# Revit family: Specialty-Equipment_TheSplashLab_Bath-Grab-Bars_GR-45-36
name_source: partatom
category: Specialty Equipment
revit_build: Autodesk Revit 2016 (Build: 20160314_0715(x64)
units: mm (PartAtom-declared; Revit-internal decimal feet)

## family parameters
Cut with Voids When Loaded = No
Host = Face
OmniClass Number = 23.40.20.21.47
OmniClass Title = Bath Grab Bars
Part Type = Normal
Room Calculation Point = No
Round Connector Dimension = Use Diameter
Shared = No

## types (5) — shared parameters
Assembly Code = E1090
AssetType = Fixed
BIMObjectName = Specialty-Equipment_TheSplashLab_Bath-Grab-Bars_GR-45-36
Category = Pr_40_30_78_05
Default Elevation = 4' - 0"
DurationUnit = Year
Manufacturer = TheSplashLab
ManufacturerName = TheSplashLab
ManufacturerURL = https://thesplashlab.com
Material = Stainless steel
Model = GR-45-36
NBSReference = Pr_40_30_78_05
Name = Specialty-Equipment_TheSplashLab_Bath-Grab-Bars_GR-45-36
NominalHeight = 0' - 3 1/2"
NominalLength = 3' - 3 1/2"
NominalWidth = 0' - 3 1/2"
Revision = 0
Uniclass2015Code = Pr_40_30_78_05
Uniclass2015Title = Bathroom furniture
Uniclass2015Version = UK_NBS_Uniclass2015_04_18
Version = 1
WarrantyDurationUnit = Year

## per-type parameters (varying)
| type | HousingMaterial |
| CS (Brushed satin stainless steel) | Brushed Stainless Steel |
| CP (Brushed copper finish) | Brushed Copper |
| BK (Brushed black finish) | Brushed Black |
| BZ (Brushed bronze finish) | Brushed Bronze |
| BR (Brushed brass finish) | Brushed Brass |

## geometry (parser evidence)
native form markers: Sweep x3
no freeform markers — native parametric forms only
